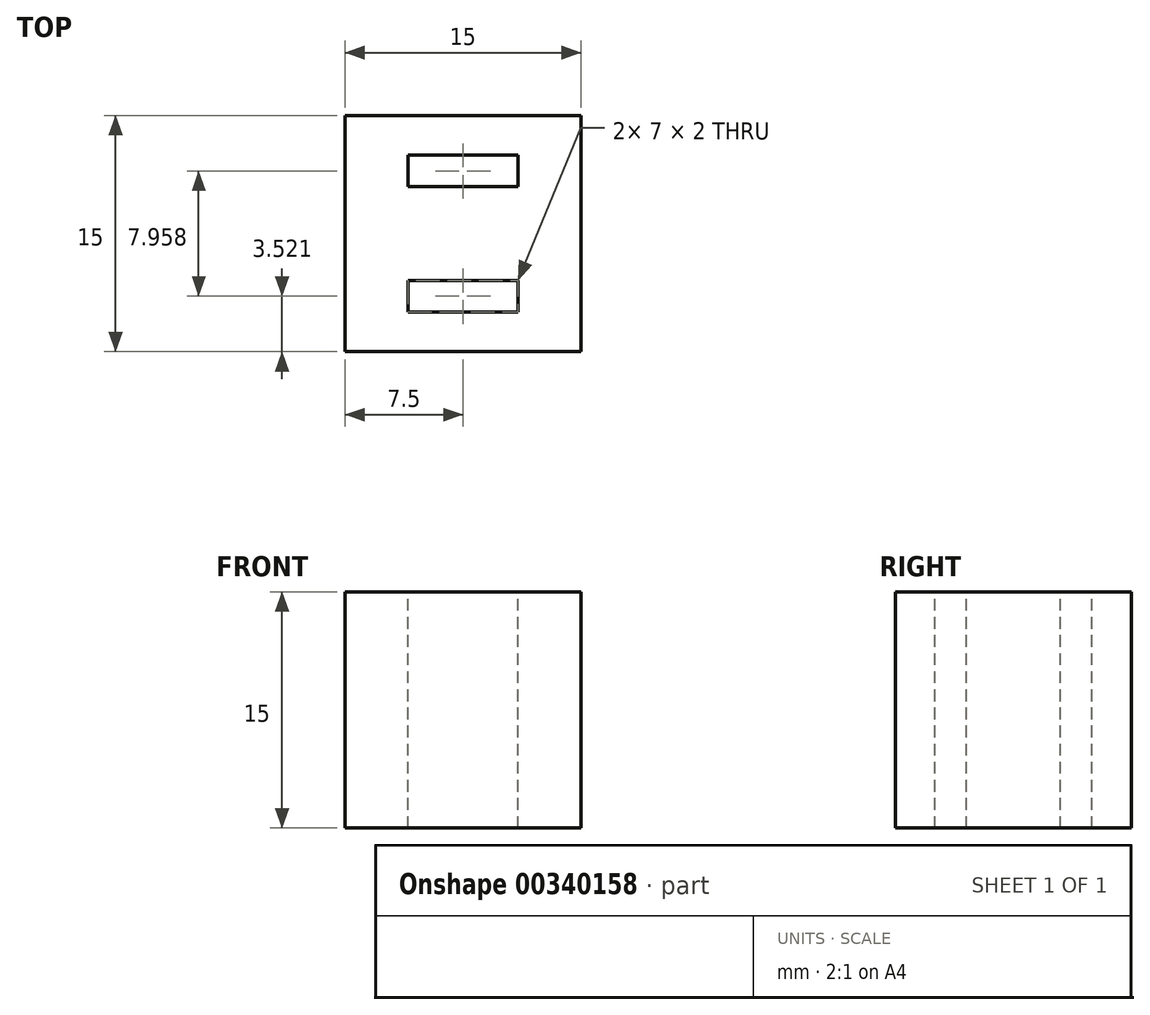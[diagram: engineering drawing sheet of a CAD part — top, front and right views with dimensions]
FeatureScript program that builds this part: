
annotation { "Feature Type Name" : "Feature", "Feature Type Description" : "" }
export const myFeature = defineFeature(function(context is Context, id is Id, definition is map)
    precondition{}
    {
        {
            var Q0;
            Q0=qCreatedBy(makeId("Top.planeOp"),FACE);
            var sketch = newSketch(context, id + "F0", { "sketchPlane" : qUnion([Q0])});
            skLineSegment(sketch, "E0.bottom", {"start": v(7.5, -7.5) * mm, "end": v(-7.5, -7.5) * mm});
            skLineSegment(sketch, "E0.top", {"start": v(7.5, 7.5) * mm, "end": v(-7.5, 7.5) * mm});
            skLineSegment(sketch, "E0.left", {"start": v(7.5, -7.5) * mm, "end": v(7.5, 7.5) * mm});
            skLineSegment(sketch, "E0.right", {"start": v(-7.5, -7.5) * mm, "end": v(-7.5, 7.5) * mm});
            skPoint(sketch, "E0.middle", {"position": v(0, 0) * mm});
            skSolve(sketch);
        }
        {
            var Q0;
            Q0 = qSketchRegion(id + "F0", true);
            extrude(context, id + "F1", {"entities" : qUnion([Q0]), "depth" : 15 * mm});
        }
        {
            var Q0;
            Q0=makeQuery(id+"F1.opExtrude","CAP_FACE",FACE,{"disambiguationData":[OSD([sQuery(id+"F0.wireOp",EDGE,"E0.bottom"),sQuery(id+"F0.wireOp",EDGE,"E0.top"),sQuery(id+"F0.wireOp",EDGE,"E0.left"),sQuery(id+"F0.wireOp",EDGE,"E0.right")])],"isStart":false});
            var sketch = newSketch(context, id + "F2", { "sketchPlane" : qUnion([Q0])});
            skLineSegment(sketch, "E1.bottom", {"start": v(3.5, 2.98) * mm, "end": v(-3.5, 2.98) * mm});
            skLineSegment(sketch, "E1.top", {"start": v(3.5, 4.98) * mm, "end": v(-3.5, 4.98) * mm});
            skLineSegment(sketch, "E1.left", {"start": v(3.5, 2.98) * mm, "end": v(3.5, 4.98) * mm});
            skLineSegment(sketch, "E1.right", {"start": v(-3.5, 2.98) * mm, "end": v(-3.5, 4.98) * mm});
            skPoint(sketch, "E1.middle", {"position": v(0, 3.98) * mm});
            skLineSegment(sketch, "E2.MirrorCS", {"start": v(3.5, -2.98) * mm, "end": v(-3.5, -2.98) * mm});
            skLineSegment(sketch, "E3.MirrorCS", {"start": v(3.5, -4.98) * mm, "end": v(-3.5, -4.98) * mm});
            skLineSegment(sketch, "E4.MirrorCS", {"start": v(3.5, -2.98) * mm, "end": v(3.5, -4.98) * mm});
            skLineSegment(sketch, "E5.MirrorCS", {"start": v(-3.5, -2.98) * mm, "end": v(-3.5, -4.98) * mm});
            skSolve(sketch);
        }
        {
            var Q0;
            Q0 = qSketchRegion(id + "F2", true);
            extrude(context, id + "F3", {"entities" : qUnion([Q0]), "operationType" : NewBodyOperationType.REMOVE, "oppositeDirection" : true, "depth" : 25 * mm});
        }
    });
